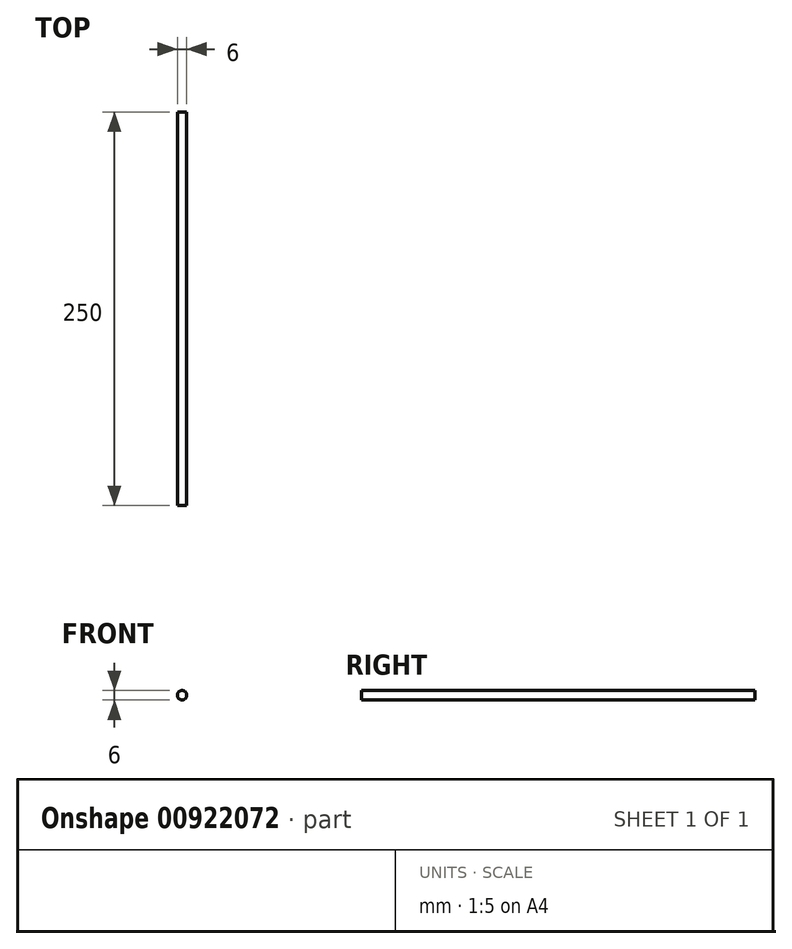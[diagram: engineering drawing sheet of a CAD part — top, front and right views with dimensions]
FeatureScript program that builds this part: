
annotation { "Feature Type Name" : "Feature", "Feature Type Description" : "" }
export const myFeature = defineFeature(function(context is Context, id is Id, definition is map)
    precondition{}
    {
        {
            var Q0;
            Q0=qCreatedBy(makeId("Front.planeOp"),FACE);
            var sketch = newSketch(context, id + "F0", { "sketchPlane" : qUnion([Q0])});
            skCircle(sketch, "E0", {"center": v(0, 0) * mm, "radius": 3 * mm});
            skSolve(sketch);
        }
        {
            var Q0;
            Q0=makeQuery(id+"F0.imprint","IMPRINT",FACE,{"disambiguationData":[TD([[makeQuery(id+"F0.imprint","IMPRINT",EDGE,{"derivedFrom":sQuery(id+"F0.wireOp",EDGE,"E0")}),1.0]])]});
            extrude(context, id + "F1", {"entities" : qUnion([Q0]), "depth" : 250 * mm, "offsetDistance" : 25 * mm});
        }
    });
